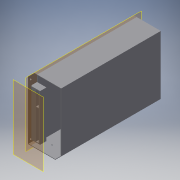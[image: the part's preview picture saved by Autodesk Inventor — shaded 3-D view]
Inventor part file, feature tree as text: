
AUTODESK INVENTOR PART (.ipt)
format: ipt  version: 2018 (Build 220112000, 112)  size: 221,696 bytes
history: native  units: mm
features: extrude x7, sketch x7, plane x3, shell x1, projected_geometry x1
ambient origin geometry x8: Origin, YZ Plane, XZ Plane, XY Plane, X Axis, Y Axis, Z Axis, Center Point
bodies: Solid1 (feature_tree)
feature tree (19):
  extrude  "Extrusion1"  Depth=50.85mm
  shell  "Shell1"  Thickness=185.0mm
  extrude  "Extrusion2"  Depth=10.9mm TaperAngle=0.0deg
  extrude  "Extrusion3"  Depth=3.0mm
  extrude  "Extrusion4"  Depth=3.0mm
  plane  "Work Plane1"
  extrude  "Extrusion5"  Depth=20.6mm
  extrude  "Extrusion6"  Depth=10.9mm TaperAngle=0.0deg
  extrude  "Extrusion7"  Depth=16.0mm
  plane  "Work Plane2"
  plane  "Work Plane3"
  sketch  "Sketch1"  dims[d0=109.3mm d1=50.85mm d2=185.0mm d3=0.0mm]
  sketch  "Sketch2"  dims[d4=1.0mm d5=10.9mm d6=0.0mm]
  projected_geometry  "Projected Loop1"
  sketch  "Sketch3"  dims[d7=19.15mm d8=3.0mm]
  sketch  "Sketch4"  dims[d9=138.3mm d10=3.0mm]
  sketch  "Sketch5"  dims[d11=14.4mm d12=20.6mm]
  sketch  "Sketch6"  dims[d13=3.0mm d14=10.9mm d15=0.0mm]
  sketch  "Sketch7"  dims[d16=4.45mm d17=7.0mm d18=3.0mm d19=6.3mm d20=3.0mm d21=56.6mm d22=14.75mm d23=9.5mm d24=3.0mm d25=3.0mm d26=116.2mm d27=6.7mm d28=3.0mm d29=9.8mm d30=9.9mm d31=3.0mm d32=14.6mm d33=3.0mm d34=10.9mm d35=0.0mm d36=10.0mm d37=12.0mm d38=50.0mm d39=5.0mm d40=1.5mm d41=0.0mm d42=1.0mm d43=16.0mm d44=0.0mm d45=1.5mm d46=2.5mm d47=27.0mm d48=8.5mm d49=1.5mm d50=1.5mm d51=16.0mm d52=0.0mm d53=25.0mm]
